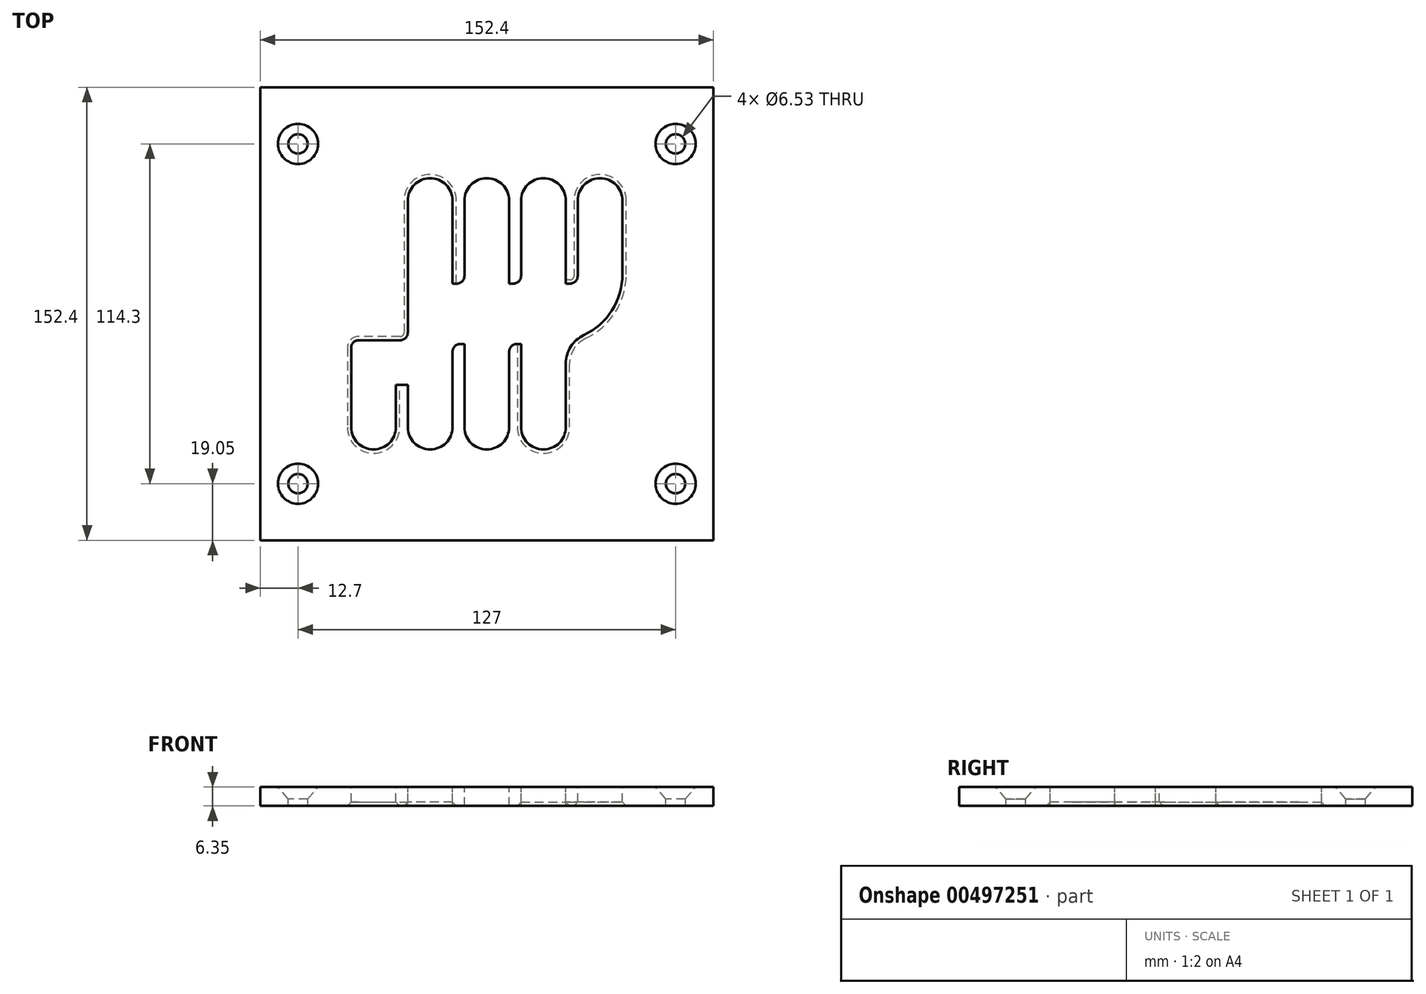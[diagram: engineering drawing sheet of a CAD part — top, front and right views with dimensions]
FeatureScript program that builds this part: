
annotation { "Feature Type Name" : "Feature", "Feature Type Description" : "" }
export const myFeature = defineFeature(function(context is Context, id is Id, definition is map)
    precondition{}
    {
        {
            var Q0;
            Q0=qCreatedBy(makeId("Top.planeOp"),FACE);
            var sketch = newSketch(context, id + "F0", { "sketchPlane" : qUnion([Q0])});
            skLineSegment(sketch, "E0.bottom", {"start": v(-76.2, 76.2) * mm, "end": v(76.2, 76.2) * mm});
            skLineSegment(sketch, "E0.top", {"start": v(-76.2, -76.2) * mm, "end": v(76.2, -76.2) * mm});
            skLineSegment(sketch, "E0.left", {"start": v(-76.2, 76.2) * mm, "end": v(-76.2, -76.2) * mm});
            skLineSegment(sketch, "E0.right", {"start": v(76.2, 76.2) * mm, "end": v(76.2, -76.2) * mm});
            skSolve(sketch);
        }
        {
            var Q0;
            Q0=makeQuery(id+"F0.imprint","IMPRINT",FACE,{"disambiguationData":[TD([[makeQuery(id+"F0.imprint","IMPRINT",EDGE,{"derivedFrom":sQuery(id+"F0.wireOp",EDGE,"E0.bottom")}),-1.0]])]});
            extrude(context, id + "F1", {"entities" : qUnion([Q0]), "depth" : 6.35 * mm});
        }
        {
            var Q0;
            Q0=makeQuery(id+"F1.opExtrude","CAP_FACE",FACE,{"disambiguationData":[OSD([sQuery(id+"F0.wireOp",EDGE,"E0.bottom"),sQuery(id+"F0.wireOp",EDGE,"E0.top"),sQuery(id+"F0.wireOp",EDGE,"E0.left"),sQuery(id+"F0.wireOp",EDGE,"E0.right")])],"isStart":false});
            var sketch = newSketch(context, id + "F2", { "sketchPlane" : qUnion([Q0])});
            skArc(sketch, "E1", {"start": v(7.53, 38.1) * mm, "mid": v(0, 45.63) * mm, "end": v(-7.53, 38.1) * mm});
            skArc(sketch, "E2", {"start": v(-11.52, 38.1) * mm, "mid": v(-19.05, 45.63) * mm, "end": v(-26.58, 38.1) * mm});
            skLineSegment(sketch, "E3", {"start": v(-26.58, 38.1) * mm, "end": v(-26.58, 0) * mm});
            skArc(sketch, "E4", {"start": v(26.58, 38.1) * mm, "mid": v(19.05, 45.63) * mm, "end": v(11.52, 38.1) * mm});
            skLineSegment(sketch, "E5", {"start": v(-26.58, 0) * mm, "end": v(-26.58, 0) * mm});
            skArc(sketch, "E6", {"start": v(-26.58, -38.1) * mm, "mid": v(-19.05, -45.63) * mm, "end": v(-11.52, -38.1) * mm});
            skArc(sketch, "E7", {"start": v(-7.53, -38.1) * mm, "mid": v(0, -45.63) * mm, "end": v(7.53, -38.1) * mm});
            skArc(sketch, "E8", {"start": v(11.52, -38.1) * mm, "mid": v(19.05, -45.63) * mm, "end": v(26.58, -38.1) * mm});
            skArc(sketch, "E9", {"start": v(-45.63, -38.1) * mm, "mid": v(-38.1, -45.63) * mm, "end": v(-30.57, -38.1) * mm});
            skArc(sketch, "E10", {"start": v(45.63, 38.1) * mm, "mid": v(38.1, 45.63) * mm, "end": v(30.57, 38.1) * mm});
            skLineSegment(sketch, "E11", {"start": v(45.63, 38.1) * mm, "end": v(45.63, 13.26) * mm});
            skLineSegment(sketch, "E12", {"start": v(-26.58, 0) * mm, "end": v(-26.58, -8.9) * mm});
            skLineSegment(sketch, "E13", {"start": v(-45.63, -8.9) * mm, "end": v(-26.58, -8.9) * mm});
            skLineSegment(sketch, "E14", {"start": v(-45.63, -38.1) * mm, "end": v(-45.63, -8.9) * mm});
            skLineSegment(sketch, "E15", {"start": v(-30.57, -38.1) * mm, "end": v(-30.57, -23.93) * mm});
            skLineSegment(sketch, "E16", {"start": v(-26.58, -38.1) * mm, "end": v(-26.58, -23.93) * mm});
            skLineSegment(sketch, "E17", {"start": v(-26.58, -23.93) * mm, "end": v(-30.57, -23.93) * mm});
            skLineSegment(sketch, "E18", {"start": v(-11.52, -10.16) * mm, "end": v(-11.52, -38.1) * mm});
            skLineSegment(sketch, "E19", {"start": v(-11.52, 38.1) * mm, "end": v(-11.52, 10.16) * mm});
            skLineSegment(sketch, "E20", {"start": v(-7.53, -10.16) * mm, "end": v(-11.52, -10.16) * mm});
            skLineSegment(sketch, "E21", {"start": v(-7.53, -38.1) * mm, "end": v(-7.53, -10.16) * mm});
            skLineSegment(sketch, "E22", {"start": v(-7.53, 38.1) * mm, "end": v(-7.53, 10.16) * mm});
            skLineSegment(sketch, "E23", {"start": v(-7.53, 10.16) * mm, "end": v(-11.52, 10.16) * mm});
            skLineSegment(sketch, "E24", {"start": v(7.53, -38.1) * mm, "end": v(7.53, -10.16) * mm});
            skLineSegment(sketch, "E25", {"start": v(7.53, -10.16) * mm, "end": v(11.52, -10.16) * mm});
            skLineSegment(sketch, "E26", {"start": v(11.52, -10.16) * mm, "end": v(11.52, -38.1) * mm});
            skLineSegment(sketch, "E27", {"start": v(26.58, -38.1) * mm, "end": v(26.58, -16.76) * mm});
            skLineSegment(sketch, "E28", {"start": v(7.53, 38.1) * mm, "end": v(7.53, 10.16) * mm});
            skLineSegment(sketch, "E29", {"start": v(7.53, 10.16) * mm, "end": v(11.52, 10.16) * mm});
            skLineSegment(sketch, "E30", {"start": v(11.52, 10.16) * mm, "end": v(11.52, 38.1) * mm});
            skLineSegment(sketch, "E31", {"start": v(26.58, 38.1) * mm, "end": v(26.58, 10.16) * mm});
            skLineSegment(sketch, "E32", {"start": v(26.58, 10.16) * mm, "end": v(30.57, 10.16) * mm});
            skLineSegment(sketch, "E33", {"start": v(30.57, 10.16) * mm, "end": v(30.57, 38.1) * mm});
            skArc(sketch, "E34", {"start": v(32.66, -7.18) * mm, "mid": v(42.11, 1.15) * mm, "end": v(45.63, 13.26) * mm});
            skArc(sketch, "E35", {"start": v(32.66, -7.18) * mm, "mid": v(28.23, -11.09) * mm, "end": v(26.58, -16.76) * mm});
            skSolve(sketch);
        }
        {
            var Q0;
            Q0 = qSketchRegion(id + "F2", true);
            extrude(context, id + "F3", {"entities" : qUnion([Q0]), "operationType" : NewBodyOperationType.REMOVE, "endBound" : BoundingType.THROUGH_ALL, "oppositeDirection" : true, "depth" : 25.4 * mm});
        }
        {
            var Q0;
            Q0=makeQuery(id+"F3.boolean.opBoolean","COPY",EDGE,{"derivedFrom":makeQuery(id+"F3.opExtrude","SWEPT_EDGE",EDGE,{"disambiguationData":[OSD([sQuery(id+"F2.wireOp",EDGE,"E22"),sQuery(id+"F2.wireOp",EDGE,"E23")])]})});
            var Q1;
            Q1=makeQuery(id+"F3.boolean.opBoolean","COPY",EDGE,{"derivedFrom":makeQuery(id+"F3.opExtrude","SWEPT_EDGE",EDGE,{"disambiguationData":[OSD([sQuery(id+"F2.wireOp",EDGE,"E18"),sQuery(id+"F2.wireOp",EDGE,"E20")])]})});
            var Q2;
            Q2=makeQuery(id+"F3.boolean.opBoolean","COPY",EDGE,{"derivedFrom":makeQuery(id+"F3.opExtrude","SWEPT_EDGE",EDGE,{"disambiguationData":[OSD([sQuery(id+"F2.wireOp",EDGE,"E24"),sQuery(id+"F2.wireOp",EDGE,"E25")])]})});
            var Q3;
            Q3=makeQuery(id+"F3.boolean.opBoolean","COPY",EDGE,{"derivedFrom":makeQuery(id+"F3.opExtrude","SWEPT_EDGE",EDGE,{"disambiguationData":[OSD([sQuery(id+"F2.wireOp",EDGE,"E29"),sQuery(id+"F2.wireOp",EDGE,"E30")])]})});
            var Q4;
            Q4=makeQuery(id+"F3.boolean.opBoolean","COPY",EDGE,{"derivedFrom":makeQuery(id+"F3.opExtrude","SWEPT_EDGE",EDGE,{"disambiguationData":[OSD([sQuery(id+"F2.wireOp",EDGE,"E32"),sQuery(id+"F2.wireOp",EDGE,"E33")])]})});
            var Q5;
            Q5=makeQuery(id+"F3.boolean.opBoolean","COPY",EDGE,{"derivedFrom":makeQuery(id+"F3.opExtrude","SWEPT_EDGE",EDGE,{"disambiguationData":[OSD([sQuery(id+"F2.wireOp",EDGE,"E12"),sQuery(id+"F2.wireOp",EDGE,"E13")])]})});
            var Q6;
            Q6=makeQuery(id+"F3.boolean.opBoolean","COPY",EDGE,{"derivedFrom":makeQuery(id+"F3.opExtrude","SWEPT_EDGE",EDGE,{"disambiguationData":[OSD([sQuery(id+"F2.wireOp",EDGE,"E13"),sQuery(id+"F2.wireOp",EDGE,"E14")])]})});
            fillet(context, id + "F4", {"entities" : qUnion([Q0, Q1, Q2, Q3, Q4, Q5, Q6]), "radius" : 2.54 * mm, "tangentPropagation" : true, "allowEdgeOverflow" : false});
        }
        {
            var Q0;
            Q0=makeQuery(id+"F3.boolean.opBoolean","COPY",EDGE,{"derivedFrom":makeQuery(id+"F3.opExtrude","CAP_EDGE",EDGE,{"disambiguationData":[OSD([sQuery(id+"F2.wireOp",EDGE,"E11")])],"isStart":true})});
            var Q1;
            Q1=makeQuery(id+"F3.boolean.opBoolean","INTERSECT",EDGE,{"derivedFrom":[makeQuery(id+"F1.opExtrude","CAP_FACE",FACE,{"disambiguationData":[OSD([sQuery(id+"F0.wireOp",EDGE,"E0.bottom"),sQuery(id+"F0.wireOp",EDGE,"E0.top"),sQuery(id+"F0.wireOp",EDGE,"E0.left"),sQuery(id+"F0.wireOp",EDGE,"E0.right")])],"isStart":true}),makeQuery(id+"F3.opExtrude","SWEPT_FACE",FACE,{"disambiguationData":[OSD([sQuery(id+"F2.wireOp",EDGE,"E33")])]})]});
            var Q2;
            Q2=makeQuery(id+"F3.boolean.opBoolean","COPY",EDGE,{"derivedFrom":makeQuery(id+"F3.opExtrude","CAP_EDGE",EDGE,{"disambiguationData":[OSD([sQuery(id+"F2.wireOp",EDGE,"E14")])],"isStart":true})});
            var Q3;
            Q3=makeQuery(id+"F3.boolean.opBoolean","INTERSECT",EDGE,{"derivedFrom":[makeQuery(id+"F1.opExtrude","CAP_FACE",FACE,{"disambiguationData":[OSD([sQuery(id+"F0.wireOp",EDGE,"E0.bottom"),sQuery(id+"F0.wireOp",EDGE,"E0.top"),sQuery(id+"F0.wireOp",EDGE,"E0.left"),sQuery(id+"F0.wireOp",EDGE,"E0.right")])],"isStart":true}),makeQuery(id+"F3.opExtrude","SWEPT_FACE",FACE,{"disambiguationData":[OSD([sQuery(id+"F2.wireOp",EDGE,"E15")])]})]});
            chamfer(context, id + "F5", {"entities" : qUnion([Q0, Q1, Q2, Q3]), "width" : 1.27 * mm, "tangentPropagation" : true});
        }
        {
            var Q0;
            Q0=makeQuery(id+"F1.opExtrude","CAP_FACE",FACE,{"disambiguationData":[OSD([sQuery(id+"F0.wireOp",EDGE,"E0.bottom"),sQuery(id+"F0.wireOp",EDGE,"E0.top"),sQuery(id+"F0.wireOp",EDGE,"E0.left"),sQuery(id+"F0.wireOp",EDGE,"E0.right")])],"isStart":false});
            var sketch = newSketch(context, id + "F6", { "sketchPlane" : qUnion([Q0])});
            skPoint(sketch, "E36", {"position": v(-63.5, 57.15) * mm});
            skPoint(sketch, "E37", {"position": v(63.5, 57.15) * mm});
            skPoint(sketch, "E38", {"position": v(63.5, -57.15) * mm});
            skPoint(sketch, "E39", {"position": v(-63.5, -57.15) * mm});
            skSolve(sketch);
        }
        {
            var Q0;
            Q0=sQuery(id+"F6.wireOp",VERTEX,"E36");
            var Q1;
            Q1=sQuery(id+"F6.wireOp",VERTEX,"E37");
            var Q2;
            Q2=sQuery(id+"F6.wireOp",VERTEX,"E38");
            var Q3;
            Q3=sQuery(id+"F6.wireOp",VERTEX,"E39");
            var Q4;
            Q4=makeQuery(id+"F1.opExtrude","SWEPT_BODY",BODY,{"disambiguationData":[OSD([sQuery(id+"F0.wireOp",EDGE,"E0.bottom"),sQuery(id+"F0.wireOp",EDGE,"E0.top"),sQuery(id+"F0.wireOp",EDGE,"E0.left"),sQuery(id+"F0.wireOp",EDGE,"E0.right")])]});
            hole(context, id + "F7", {"style" : HoleStyle.C_SINK, "endStyle" : HoleEndStyle.THROUGH, "holeDiameter" : 6.53 * mm, "cSinkDiameter" : 13.5 * mm, "cSinkAngle" : 82 * degree, "isTappedThrough" : true, "tappedDepth" : 12.7 * mm, "tapClearance" : 3, "startFromSketch" : true, "locations" : qUnion([Q0, Q1, Q2, Q3]), "scope" : qUnion([Q4])});
        }
    });
